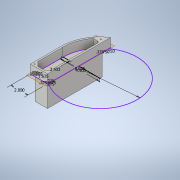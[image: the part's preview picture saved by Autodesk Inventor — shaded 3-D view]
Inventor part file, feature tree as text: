
AUTODESK INVENTOR PART (.ipt)
format: ipt  version: 2021 (Build 250183000, 183)  size: 192,000 bytes
history: native  units: in
note: dims shown in document units (in); Inventor stores cm internally (conversion verified against a paired STEP export)
features: sketch x3, extrude x3, fillet x3, plane x1, hole x1
ambient origin geometry x8: Origin, YZ Plane, XZ Plane, XY Plane, X Axis, Y Axis, Z Axis, Center Point
bodies: Solid1 (feature_tree)
feature tree (11):
  sketch  "Sketch1"  dims[d2=2.0in d10=8.625in]
  extrude  "Extrusion1"  Depth=8.625in
  plane  "Work Plane1"
  hole  "Hole2"  [1 undecoded]
  extrude  "Extrusion2"  Depth=0.5in
  extrude  "Extrusion3"  Depth=0.25in
  fillet  "Fillet3"  Radius=0.375in
  sketch  "Sketch4"  dims[d14=0.5in d15=0.5in d16=0.375in d17=0.375in d18=0.75in d19=0.25in d20=0.25in d21=0.275in d22=0.275in d23=0.75in d24=0.375in d25=1.0in d26=0.0in d34=-1.0in d35=0.9375in d36=0.5in d37=0.125in d38=0.129in d39=0.75in d40=0.199in d41=0.25in d42=0.5635in d43=1.0in d44=0.8108in d45=2.5in d46=0.0in d47=0.25in d48=0.25in d49=0.25in d50=0.25in d51=0.125in d52=0.0in d55=0.5in d57=4.5in d58=0.5in d59=0.25in d60=0.25in]
  fillet  "Fillet4"  Radius=0.75in
  fillet  "Fillet5"  Radius=0.25in
  sketch  "Sketch3"  dims[d11=3.4325in d13=1.625in]
note: 1 required parameter value undecoded (feature->parameter linkage not recoverable at this tier; creation-order binding heuristic only, values carry confidence <= 0.55)
